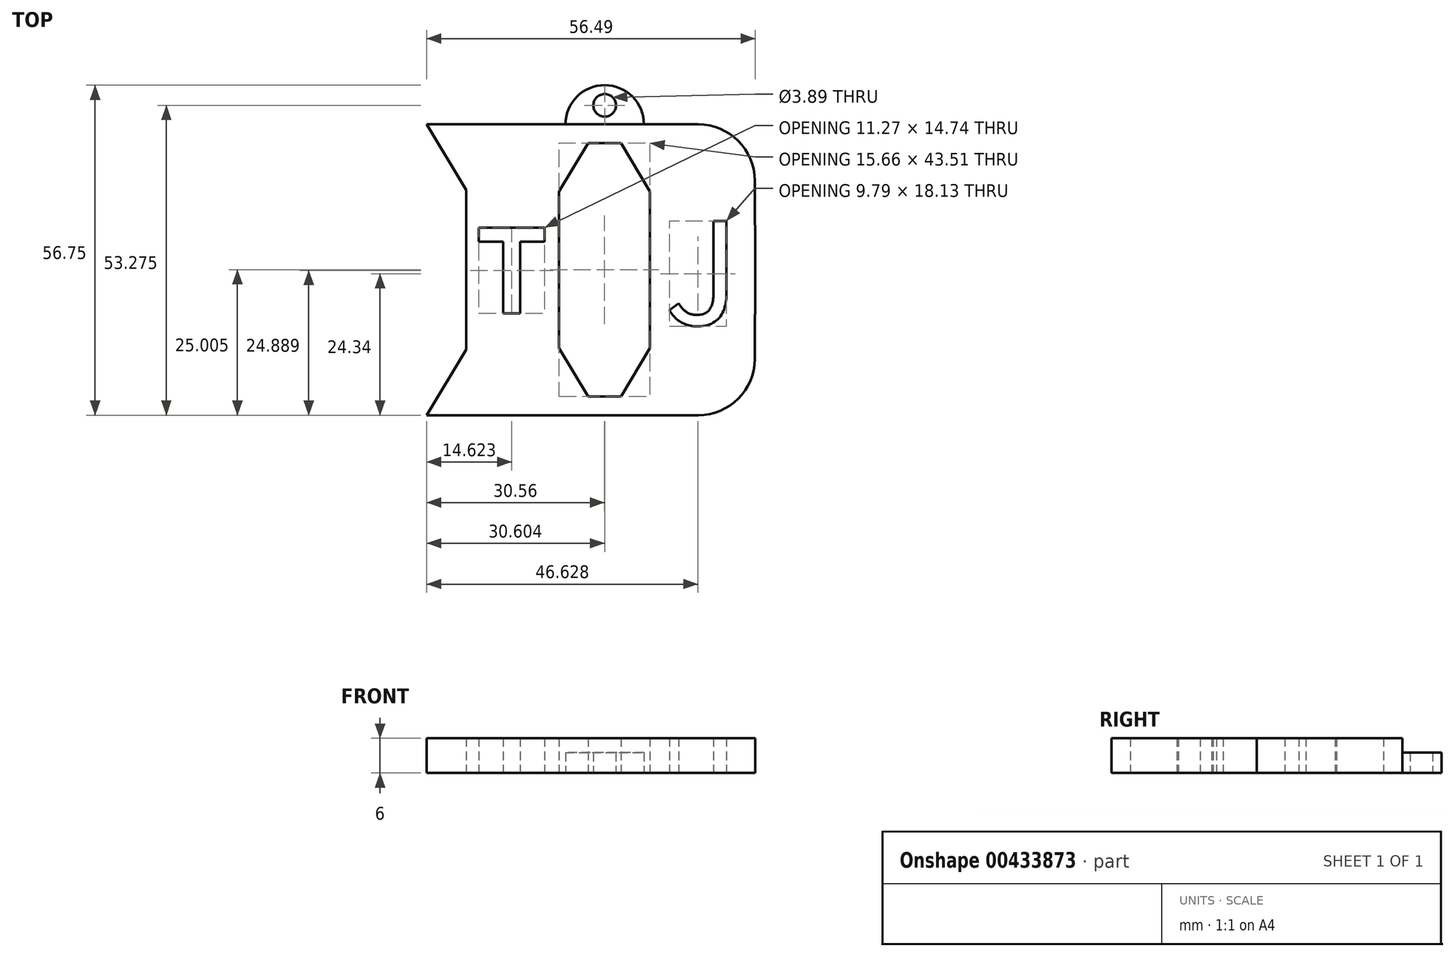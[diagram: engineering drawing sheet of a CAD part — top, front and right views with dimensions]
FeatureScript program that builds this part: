
annotation { "Feature Type Name" : "Feature", "Feature Type Description" : "" }
export const myFeature = defineFeature(function(context is Context, id is Id, definition is map)
    precondition{}
    {
        {
            var Q0;
            Q0=qCreatedBy(makeId("Top.planeOp"),FACE);
            var sketch = newSketch(context, id + "F0", { "sketchPlane" : qUnion([Q0])});
            skLineSegment(sketch, "E0", {"start": v(-29.78, -23.49) * mm, "end": v(0, -23.49) * mm});
            skPoint(sketch, "E1.endSnap0", {"position": v(16.88, 1.51) * mm});
            skArc(sketch, "E2", {"start": v(16.88, -23.49) * mm, "mid": v(23.75, -20.65) * mm, "end": v(26.63, -13.79) * mm});
            skLineSegment(sketch, "E3", {"start": v(26.63, -13.79) * mm, "end": v(26.71, 1.51) * mm});
            skLineSegment(sketch, "E4", {"start": v(-1.98, -20.24) * mm, "end": v(-7.05, -11.95) * mm});
            skLineSegment(sketch, "E5", {"start": v(-7.05, -11.95) * mm, "end": v(-7.05, 1.51) * mm});
            skLineSegment(sketch, "E6", {"start": v(3.6, -20.24) * mm, "end": v(8.61, -11.97) * mm});
            skLineSegment(sketch, "E7", {"start": v(8.61, -11.97) * mm, "end": v(8.61, 1.51) * mm});
            skLineSegment(sketch, "E8", {"start": v(-29.78, -23.49) * mm, "end": v(-22.95, -12.19) * mm});
            skLineSegment(sketch, "E9", {"start": v(-22.95, -12.19) * mm, "end": v(-22.95, 1.51) * mm});
            skLineSegment(sketch, "E10.MirrorCS", {"start": v(-22.95, 15.22) * mm, "end": v(-22.95, 1.51) * mm});
            skLineSegment(sketch, "E11.MirrorCS", {"start": v(-29.78, 26.51) * mm, "end": v(-22.95, 15.22) * mm});
            skLineSegment(sketch, "E12.MirrorCS", {"start": v(-29.78, 26.51) * mm, "end": v(0, 26.51) * mm});
            skLineSegment(sketch, "E13.MirrorCS", {"start": v(-7.05, 14.98) * mm, "end": v(-7.05, 1.51) * mm});
            skLineSegment(sketch, "E14.MirrorCS", {"start": v(-1.98, 23.27) * mm, "end": v(-7.05, 14.98) * mm});
            skLineSegment(sketch, "E15.MirrorCS", {"start": v(3.6, 23.27) * mm, "end": v(8.61, 15) * mm});
            skLineSegment(sketch, "E16.MirrorCS", {"start": v(8.61, 15) * mm, "end": v(8.61, 1.51) * mm});
            skLineSegment(sketch, "E17.MirrorCS", {"start": v(26.63, 16.82) * mm, "end": v(26.71, 1.51) * mm});
            skArc(sketch, "E18.MirrorCS", {"start": v(16.88, 26.51) * mm, "mid": v(23.75, 23.68) * mm, "end": v(26.63, 16.82) * mm});
            skLineSegment(sketch, "E19", {"start": v(-22.95, 1.51) * mm, "end": v(26.71, 1.51) * mm});
            skArc(sketch, "E20", {"start": v(7.57, 26.51) * mm, "mid": v(0.82, 33.26) * mm, "end": v(-5.92, 26.51) * mm});
            skCircle(sketch, "E21", {"center": v(0.82, 29.79) * mm, "radius": 1.95 * mm});
            skLineSegment(sketch, "E22.trimOffspring", {"start": v(1.65, 26.51) * mm, "end": v(16.88, 26.51) * mm});
            skLineSegment(sketch, "E23.trimOffspring", {"start": v(1.65, -23.49) * mm, "end": v(16.88, -23.49) * mm});
            skPoint(sketch, "E24.MirrorCS.end.orphan", {"position": v(-5.92, -23.49) * mm});
            skPoint(sketch, "E24.MirrorCS.start.orphan", {"position": v(7.57, -23.49) * mm});
            skLineSegment(sketch, "E25", {"start": v(0, -23.49) * mm, "end": v(1.65, -23.49) * mm});
            skLineSegment(sketch, "E26", {"start": v(0, 26.51) * mm, "end": v(1.65, 26.51) * mm});
            skLineSegment(sketch, "E27", {"start": v(-1.98, 23.27) * mm, "end": v(3.6, 23.27) * mm});
            skPoint(sketch, "E28.orphan", {"position": v(-1.03, 24.83) * mm});
            skPoint(sketch, "E29.orphan", {"position": v(2.66, 24.83) * mm});
            skLineSegment(sketch, "E30.MirrorCS", {"start": v(-1.98, -20.24) * mm, "end": v(3.6, -20.24) * mm});
            skPoint(sketch, "E31.MirrorCS.start.orphan", {"position": v(-1.03, -21.8) * mm});
            skPoint(sketch, "E32.orphan", {"position": v(2.66, -21.8) * mm});
            skText(sketch, "E33", { "text": "T", "fontName": "NotoSansCJKsc-Bold.otf"});
            skText(sketch, "E34", { "text": "J", "fontName": "NotoSansCJKsc-Regular.otf"});
            const initialGuessF0  = {"E33": [-0.02139, -0.00597, 1, 0, 0.01434], "E34": [0.0111, -0.0079, 1, 0, 0.0175]};
            skSetInitialGuess(sketch, initialGuessF0);
            skSolve(sketch);
        }
        {
            var Q0;
            {var subQ0=sQuery(id+"F0.wireOp",EDGE,"E15.MirrorCS");Q0=makeQuery(id+"F0.imprint","IMPRINT",FACE,{"disambiguationData":[TD([[makeQuery(id+"F0.imprint","IMPRINT",EDGE,{"derivedFrom":subQ0}),1.0]])]});}
            var Q1;
            {var subQ6=sQuery(id+"F0.wireOp",EDGE,"E10.MirrorCS");Q1=makeQuery(id+"F0.imprint","IMPRINT",FACE,{"disambiguationData":[TD([[makeQuery(id+"F0.imprint","IMPRINT",EDGE,{"derivedFrom":subQ6}),1.0]])]});}
            var Q2;
            {var subQ1=sQuery(id+"F0.wireOp",EDGE,"E2");Q2=makeQuery(id+"F0.imprint","IMPRINT",FACE,{"disambiguationData":[TD([[makeQuery(id+"F0.imprint","IMPRINT",EDGE,{"derivedFrom":subQ1}),1.0]])]});}
            var Q3;
            {var subQ1=sQuery(id+"F0.wireOp",EDGE,"E4");Q3=makeQuery(id+"F0.imprint","IMPRINT",FACE,{"disambiguationData":[TD([[makeQuery(id+"F0.imprint","IMPRINT",EDGE,{"derivedFrom":subQ1}),1.0]])]});}
            var Q4;
            {var subQ2=sQuery(id+"F0.wireOp",EDGE,"E24.MirrorCS");Q4=makeQuery(id+"F0.imprint","IMPRINT",FACE,{"disambiguationData":[TD([[makeQuery(id+"F0.imprint","IMPRINT",EDGE,{"derivedFrom":subQ2}),-1.0]])]});}
            var Q5;
            {var subQ1=sQuery(id+"F0.wireOp",EDGE,"mLoYcLzS-eiOT-QkwH-DPjM-P5kjOfTnDSYI");Q5=makeQuery(id+"F0.imprint","IMPRINT",FACE,{"disambiguationData":[TD([[makeQuery(id+"F0.imprint","IMPRINT",EDGE,{"derivedFrom":subQ1}),1.0]])]});}
            extrude(context, id + "F1", {"entities" : qUnion([Q0, Q1, Q2, Q3, Q4, Q5]), "depth" : 6 * mm, "offsetDistance" : 25 * mm});
        }
        {
            var Q0;
            {var subQ1=sQuery(id+"F0.wireOp",EDGE,"E20");Q0=makeQuery(id+"F0.imprint","IMPRINT",FACE,{"disambiguationData":[TD([[makeQuery(id+"F0.imprint","IMPRINT",EDGE,{"derivedFrom":subQ1}),1.0]])]});}
            extrude(context, id + "F2", {"entities" : qUnion([Q0]), "operationType" : NewBodyOperationType.ADD, "depth" : 3.5 * mm, "offsetDistance" : 25 * mm});
        }
    });
